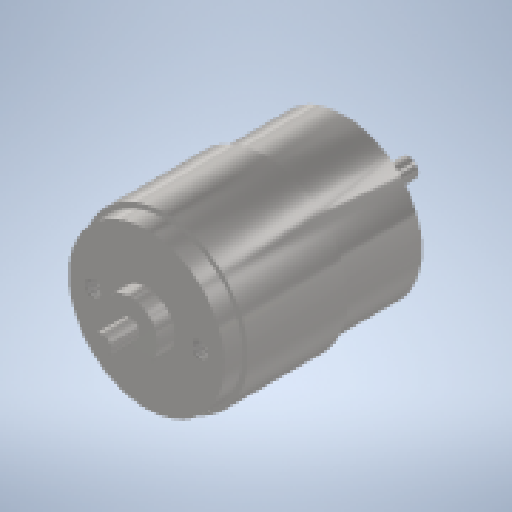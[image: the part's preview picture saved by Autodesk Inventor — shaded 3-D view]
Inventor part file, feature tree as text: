
AUTODESK INVENTOR PART (.ipt)
format: ipt  version: 2024 (Build 280153000, 153)  size: 189,952 bytes
history: native  units: mm
features: thread x2, sketch x2, other x1, revolve x1, hole x1
ambient origin geometry x8: Origin, YZ Plane, XZ Plane, XY Plane, X Axis, Y Axis, Z Axis, Center Point
bodies: Body1 (feature_tree)
feature tree (7):
  other  "ソリッド1"
  revolve  "回転1"
  hole  "穴1"  [1 undecoded]
  thread  "ねじ1"
  thread  "ねじ2"
  sketch  "スケッチ1"
  sketch  "スケッチ2"
note: 1 required parameter value undecoded (feature->parameter linkage not recoverable at this tier; creation-order binding heuristic only, values carry confidence <= 0.55)
